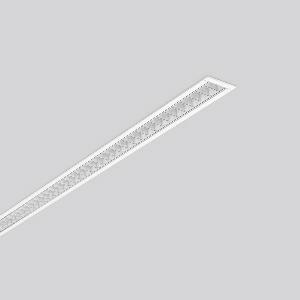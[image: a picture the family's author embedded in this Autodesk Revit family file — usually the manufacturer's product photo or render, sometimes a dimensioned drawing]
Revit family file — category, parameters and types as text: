
# Revit family: less_is_more_27_312177_002_2acf
name_source: partatom
category: Lighting Fixtures
units: mm (PartAtom-declared; Revit-internal decimal feet)

## family parameters
Cut with Voids When Loaded = No
Host = Face
Light Source = No
Part Type = Normal
Room Calculation Point = No
Round Connector Dimension = Use Diameter
Shared = No

## types (1)
- LESS IS MORE 27 (1 x LED Modul 830, 2350 lm, 3000)
    Apparent Load = 29 VA
    CIE Flux Codes = 90 99 100 100 100
    Color Rendering = 80
    Color Temperature = 3000
    Default Elevation = 1800 mm
    Description = Series: LESS IS MORE 27
Recessed ceiling and wall luminaire with slim design. Housing: extruded aluminium profile, powder-coated. End cap aluminium powder-coated. High polish aluminium micro grid. Perfect for office areas (RUG < 19) and environments with computer screens in accordance with EN 12464-1. Suitable for Recessed ceiling mounting, wall (recessed). External driver with connecting cable. 
Colour: traffic white, matt (RAL 9016)
Length: 1014 mm
Width: 38 mm
Height: 2 mm
Cut-out length: 1006 mm
Cut-out width: 30 mm
Recess height: 45-60 mm
Luminaire: recess height: 37 mm
Lamp: LED
Socket: without socket
Colour temperature: 3000K
Colour rendering index (CRI): 82
System power: 29 W
Rated luminous flux: 2350 lm
Luminous efficiency: 81 lm/W
Control gear: Regulated power supply
Protection class: II
Type of protection: IP 20
    Height = 0 mm  [stored 0 ft]
    Lamp = 1 x LED Modul 830
    Lamp Light Flux = 2350 lm
    Lamp count = 1
    Length = 1014 mm
    Lifetime = 50000 h
    Luminous efficacy = 81 lm/W
    Manufacturer = RZB
    ModVariant = No
    Model = 312177.002
    Mounting Place = Ceiling, Wall
    Mounting Type = Recessed
    Number of Poles = 1
    OnlyDefault = Yes
    Power Factor = 1
    Product Name = LESS IS MORE 27
    Product group = Recessed LED linear luminaires
    ProductGroupID = 407
    Protection Class = Protection class II
    Protection Degree = IP 20
    RLX_Detail_Level = 1
    RLX_Emergency_Light_Flux = 0 lm
    RLX_Emergency_Type = 0
    RLX_Emergency_Type_DB = No
    RlxData = <blob elided: 27013 chars, md5=3f9cfe60>
    Socket = socket
    Standby Power = 0 W
    System Light Flux = 2350 lm
    System Power = 29 W
    Type Comments = Product without accessories
    Type Image = 312177.002.jpg
    URL = http://relux.com
    VarID = ---
    Voltage = 230 V
    Voltage Range = 220-240 V
    Weight = 0.00 kg
    Width = 38 mm

note: [stored X ft] marks values corroborated as IEEE doubles in the binary element streams (Revit-internal decimal feet)

## geometry (parser evidence)
native form markers: Blend x4, Sweep x12
no freeform markers — native parametric forms only
